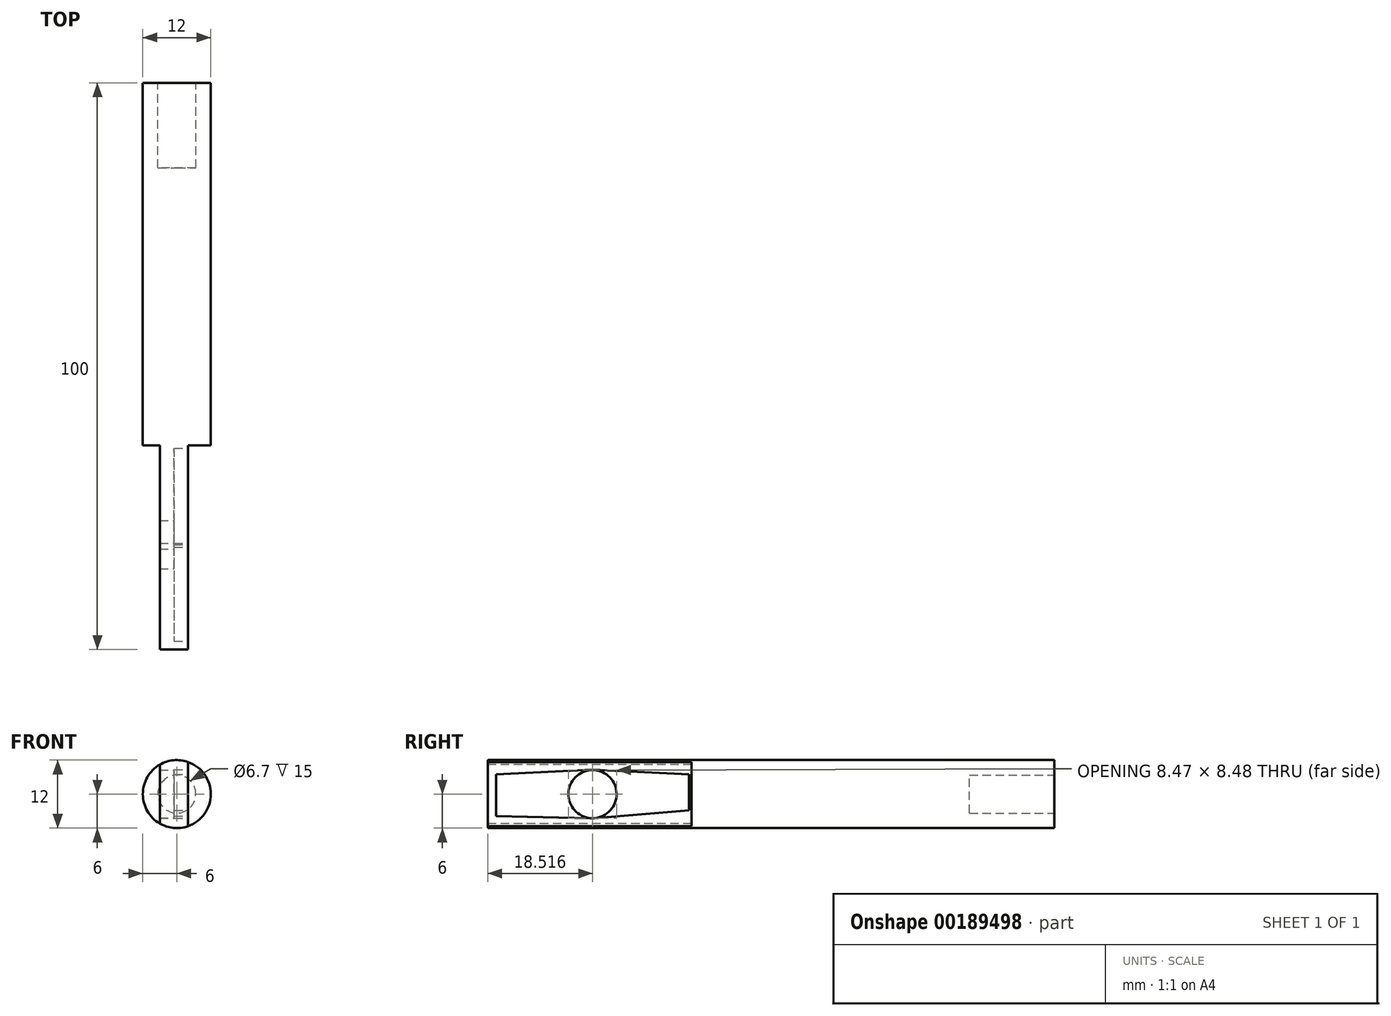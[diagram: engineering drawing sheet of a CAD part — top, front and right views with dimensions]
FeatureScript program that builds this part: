
annotation { "Feature Type Name" : "Feature", "Feature Type Description" : "" }
export const myFeature = defineFeature(function(context is Context, id is Id, definition is map)
    precondition{}
    {
        {
            var Q0;
            Q0=qCreatedBy(makeId("Front.planeOp"),FACE);
            var sketch = newSketch(context, id + "F0", { "sketchPlane" : qUnion([Q0])});
            skCircle(sketch, "E0", {"center": v(0, 0) * mm, "radius": 6 * mm});
            skSolve(sketch);
        }
        {
            var Q0;
            Q0=qCreatedBy(makeId("Front.planeOp"),FACE);
            var sketch = newSketch(context, id + "F1", { "sketchPlane" : qUnion([Q0])});
            skCircle(sketch, "E1", {"center": v(0, 0) * mm, "radius": 3.35 * mm});
            skSolve(sketch);
        }
        {
            var Q0;
            Q0 = qSketchRegion(id + "F0", true);
            extrude(context, id + "F2", {"entities" : qUnion([Q0]), "depth" : 100 * mm});
        }
        {
            var Q0;
            Q0 = qSketchRegion(id + "F1", true);
            extrude(context, id + "F3", {"entities" : qUnion([Q0]), "operationType" : NewBodyOperationType.REMOVE, "depth" : 15 * mm});
        }
        {
            var Q0;
            Q0=makeQuery(id+"F2.opExtrude","CAP_FACE",FACE,{"disambiguationData":[OSD([sQuery(id+"F0.wireOp",EDGE,"E0")])],"isStart":false});
            var sketch = newSketch(context, id + "F4", { "sketchPlane" : qUnion([Q0])});
            skLineSegment(sketch, "E2.bottom", {"start": v(-3, -6) * mm, "end": v(2, -6) * mm});
            skLineSegment(sketch, "E2.top", {"start": v(-3, 6) * mm, "end": v(2, 6) * mm});
            skLineSegment(sketch, "E2.left", {"start": v(-3, -6) * mm, "end": v(-3, 6) * mm});
            skLineSegment(sketch, "E2.right", {"start": v(2, -6) * mm, "end": v(2, 6) * mm});
            skSolve(sketch);
        }
        {
            var Q0;
            {var subQ0=sQuery(id+"F4.wireOp",EDGE,"E2.left");var subQ1=makeQuery(id+"F2.opExtrude","CAP_EDGE",EDGE,{"disambiguationData":[OSD([sQuery(id+"F0.wireOp",EDGE,"E0")])],"isStart":false});var subQ2=makeQuery(id+"F4.imprint","INTERSECT",VERTEX,{"disambiguationData":[OD(0.0)],"derivedFrom":[subQ1,subQ0]});Q0=makeQuery(id+"F4.imprint","IMPRINT",FACE,{"disambiguationData":[TD([[makeQuery(id+"F4.imprint","IMPRINT",EDGE,{"disambiguationData":[TD([[subQ2,-1.0]])],"derivedFrom":subQ0}),1.0]])]});}
            var Q1;
            {var subQ0=sQuery(id+"F4.wireOp",EDGE,"E2.right");var subQ1=makeQuery(id+"F2.opExtrude","CAP_EDGE",EDGE,{"disambiguationData":[OSD([sQuery(id+"F0.wireOp",EDGE,"E0")])],"isStart":false});var subQ2=makeQuery(id+"F4.imprint","INTERSECT",VERTEX,{"disambiguationData":[OD(0.0)],"derivedFrom":[subQ1,subQ0]});Q1=makeQuery(id+"F4.imprint","IMPRINT",FACE,{"disambiguationData":[TD([[makeQuery(id+"F4.imprint","IMPRINT",EDGE,{"disambiguationData":[TD([[subQ2,-1.0]])],"derivedFrom":subQ0}),-1.0]])]});}
            extrude(context, id + "F5", {"entities" : qUnion([Q0, Q1]), "operationType" : NewBodyOperationType.REMOVE, "oppositeDirection" : true, "depth" : 36 * mm});
        }
        {
            var Q0;
            Q0=makeQuery(id+"F5.boolean.opBoolean","COPY",FACE,{"derivedFrom":makeQuery(id+"F5.opExtrude","SWEPT_FACE",FACE,{"disambiguationData":[OSD([sQuery(id+"F4.wireOp",EDGE,"E2.right")])]})});
            var sketch = newSketch(context, id + "F6", { "sketchPlane" : qUnion([Q0])});
            skLineSegment(sketch, "E3.right", {"start": v(-64.5, 1.71) * mm, "end": v(-64.5, -1.71) * mm});
            skPoint(sketch, "E4", {"position": v(-44.74, 3.52) * mm});
            skPoint(sketch, "E5", {"position": v(-98.5, 1.55) * mm});
            skPoint(sketch, "E6", {"position": v(-81.5, 3.52) * mm});
            skPoint(sketch, "E7", {"position": v(-64.5, 1.71) * mm});
            skPoint(sketch, "E8", {"position": v(-83.89, 3.52) * mm});
            skPoint(sketch, "E9.MirrorP", {"position": v(-64.5, -1.71) * mm});
            skPoint(sketch, "E10.orphan", {"position": v(-98.5, 3.52) * mm});
            skPoint(sketch, "E11.orphan", {"position": v(-98.5, -3.18) * mm});
            skPoint(sketch, "E12.orphan", {"position": v(-64.5, -2.86) * mm});
            skPoint(sketch, "E13.orphan", {"position": v(-64.5, 3.52) * mm});
            skPoint(sketch, "E14.end.orphan", {"position": v(-88.62, -2.86) * mm});
            skPoint(sketch, "E15.end.orphan", {"position": v(-74.05, -2.86) * mm});
            skPoint(sketch, "E16.orphan", {"position": v(-83.6, -2.86) * mm});
            skPoint(sketch, "E17.center.orphan", {"position": v(-81.5, 0) * mm});
            skLineSegment(sketch, "E18", {"start": v(-83.89, 3.52) * mm, "end": v(-83.89, 3.52) * mm});
            skLineSegment(sketch, "E19", {"start": v(-83.89, -3.52) * mm, "end": v(-83.89, -3.52) * mm});
            skCircle(sketch, "E20", {"center": v(-81.5, 0) * mm, "radius": 4.25 * mm});
            skPoint(sketch, "E21.trimOffspring.end.orphan", {"position": v(-44.74, -3.52) * mm});
            skLineSegment(sketch, "E22.top", {"start": v(-81.74, -4.24) * mm, "end": v(-81.24, -4.24) * mm});
            skLineSegment(sketch, "E22.right", {"start": v(-64.5, 3.52) * mm, "end": v(-64.5, -2.86) * mm});
            skPoint(sketch, "E23", {"position": v(-81.5, 4.28) * mm});
            skLineSegment(sketch, "E24", {"start": v(-81.5, 4.28) * mm, "end": v(-64.5, 3.52) * mm});
            skLineSegment(sketch, "E25", {"start": v(-64.5, -2.86) * mm, "end": v(-81.24, -4.24) * mm});
            skPoint(sketch, "E26.orphan", {"position": v(-64.5, -4.24) * mm});
            skLineSegment(sketch, "E27", {"start": v(-81.5, 4.28) * mm, "end": v(-98.5, 3.52) * mm});
            skLineSegment(sketch, "E28", {"start": v(-81.24, -4.24) * mm, "end": v(-82.27, -4.18) * mm});
            skPoint(sketch, "E3.left.end.orphan", {"position": v(-98.5, -1.55) * mm});
            skLineSegment(sketch, "E29", {"start": v(-98.5, 3.52) * mm, "end": v(-98.5, -3.18) * mm});
            skLineSegment(sketch, "E30", {"start": v(-98.5, -3.18) * mm, "end": v(-98.5, -3.9) * mm});
            skLineSegment(sketch, "E31", {"start": v(-81.24, -4.24) * mm, "end": v(-98.5, -3.9) * mm});
            skSolve(sketch);
        }
        {
            var Q0;
            Q0 = qSketchRegion(id + "F6", true);
            extrude(context, id + "F7", {"entities" : qUnion([Q0]), "operationType" : NewBodyOperationType.REMOVE, "oppositeDirection" : true, "depth" : 2.5 * mm});
        }
        {
            var Q0;
            {var subQ0=sQuery(id+"F6.wireOp",EDGE,"E20");var subQ1=makeQuery(id+"F6.imprint","INTERSECT",VERTEX,{"derivedFrom":[sQuery(id+"F6.wireOp",EDGE,"E18"),subQ0]});Q0=makeQuery(id+"F6.imprint","IMPRINT",FACE,{"disambiguationData":[TD([[makeQuery(id+"F6.imprint","IMPRINT",EDGE,{"disambiguationData":[TD([[subQ1,-1.0]])],"derivedFrom":subQ0}),1.0]])]});}
            extrude(context, id + "F8", {"entities" : qUnion([Q0]), "operationType" : NewBodyOperationType.REMOVE, "oppositeDirection" : true, "depth" : 25 * mm});
        }
    });
